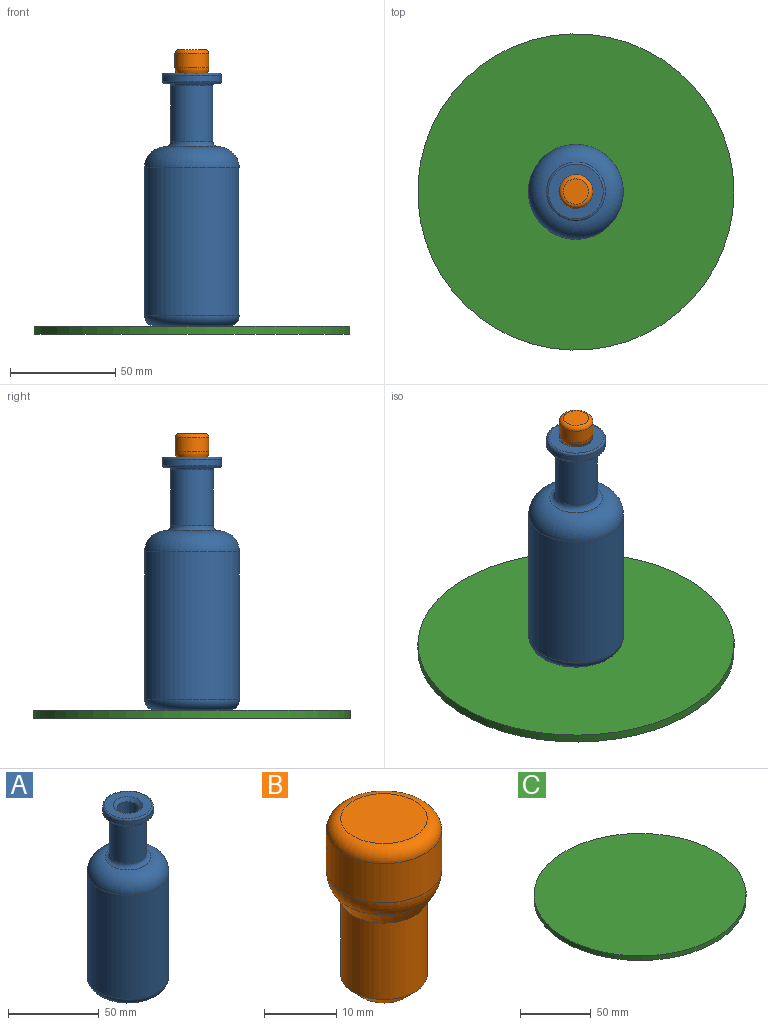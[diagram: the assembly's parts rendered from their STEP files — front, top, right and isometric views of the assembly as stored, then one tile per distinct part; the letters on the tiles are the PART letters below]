
ASSEMBLY  parts=3 mates=4
PART A: 15 faces, bbox 48.7x48.7x120 mm
  f0: cylinder r=10mm len=26.5mm, axis (0,0,-1), area 1665mm2, adj f8,f12
  f1: cylinder r=22.5mm len=70mm, axis (0,0,-1), area 9896mm2, adj f9,f14
  f2: plane 35x35mm, normal (0,0,-1), area 962.1mm2, adj f14
  f3: plane 12x12mm, normal (0,0,1), area 113.1mm2, adj f4
  f4: cylinder r=6mm len=33mm, axis (0,0,-1), area 1244.1mm2, adj f3,f13
  f5: plane 26x26mm, normal (0,0,1), area 329.9mm2, adj f10,f13
  f6: cylinder r=14mm len=28mm, axis (0,0,-1), area 263.9mm2, adj f10,f11
  f7: plane 26x26mm, normal (0,0,-1), area 150.8mm2, adj f11,f12
  f8: torus R=12.5mm, axis (0,0,-1), area 269.2mm2, adj f0,f9
  f9: torus R=12.5mm, axis (0,0,-1), area 1862mm2, adj f1,f8
  f10: torus R=13mm, axis (0,0,-1), area 134.6mm2, adj f5,f6
  f11: torus R=13mm, axis (0,0,-1), area 134.6mm2, adj f6,f7
  f12: torus R=11mm, axis (0,0,-1), area 102.3mm2, adj f0,f7
  f13: cone r=8mm half-angle=45deg, axis (0,0,1), area 124.4mm2, adj f4,f5
  f14: torus R=17.5mm, axis (0,0,-1), area 1020.7mm2, adj f1,f2
PART B: 8 faces, bbox 17.3x17.3x28.5 mm
  f0: plane 12x12mm, normal (0,0,1), area 113.1mm2, adj f5
  f1: cylinder r=8mm len=16mm, axis (0,0,1), area 335.8mm2, adj f5,f7
  f2: cone r=8mm half-angle=29.6deg, axis (0,0,1), area 114.6mm2, adj f3,f7
  f3: cylinder r=6mm len=13mm, axis (0,0,1), area 490.1mm2, adj f2,f6
  f4: plane 8x8mm, normal (0,0,-1), area 50.3mm2, adj f6
  f5: torus R=6mm, axis (0,0,-1), area 143.6mm2, adj f0,f1
  f6: cone r=6mm half-angle=45deg, axis (0,0,1), area 88.9mm2, adj f3,f4
  f7: torus R=3mm, axis (0,0,-1), area 126.2mm2, adj f1,f2
PART C: 3 faces, bbox 150x150x4 mm
  f0: cylinder r=75mm len=150mm, axis (0,0,-1), area 1885mm2, adj f1,f2
  f1: plane 150x150mm, normal (0,0,1), area 17671.5mm2, adj f0
  f2: plane 150x150mm, normal (0,0,-1), area 17671.5mm2, adj f0
PLACE A t=(0,0,-40)mm
PLACE B t=(0,0,62.62)mm
PLACE C t=(0,0,-44)mm
MATE planar C.f0 <-> A.f0  axis (0,0,1) through (0,0,-40)mm
MATE cylindrical A.f0 <-> C.f0  axis (0,0,-1) through (0,0,0)mm
MATE planar B.f1 <-> A.f0  axis (0,0,1) through (0,0,80)mm
MATE cylindrical B.f1 <-> A.f0  axis (0,0,1) through (0,0,71.12)mm
